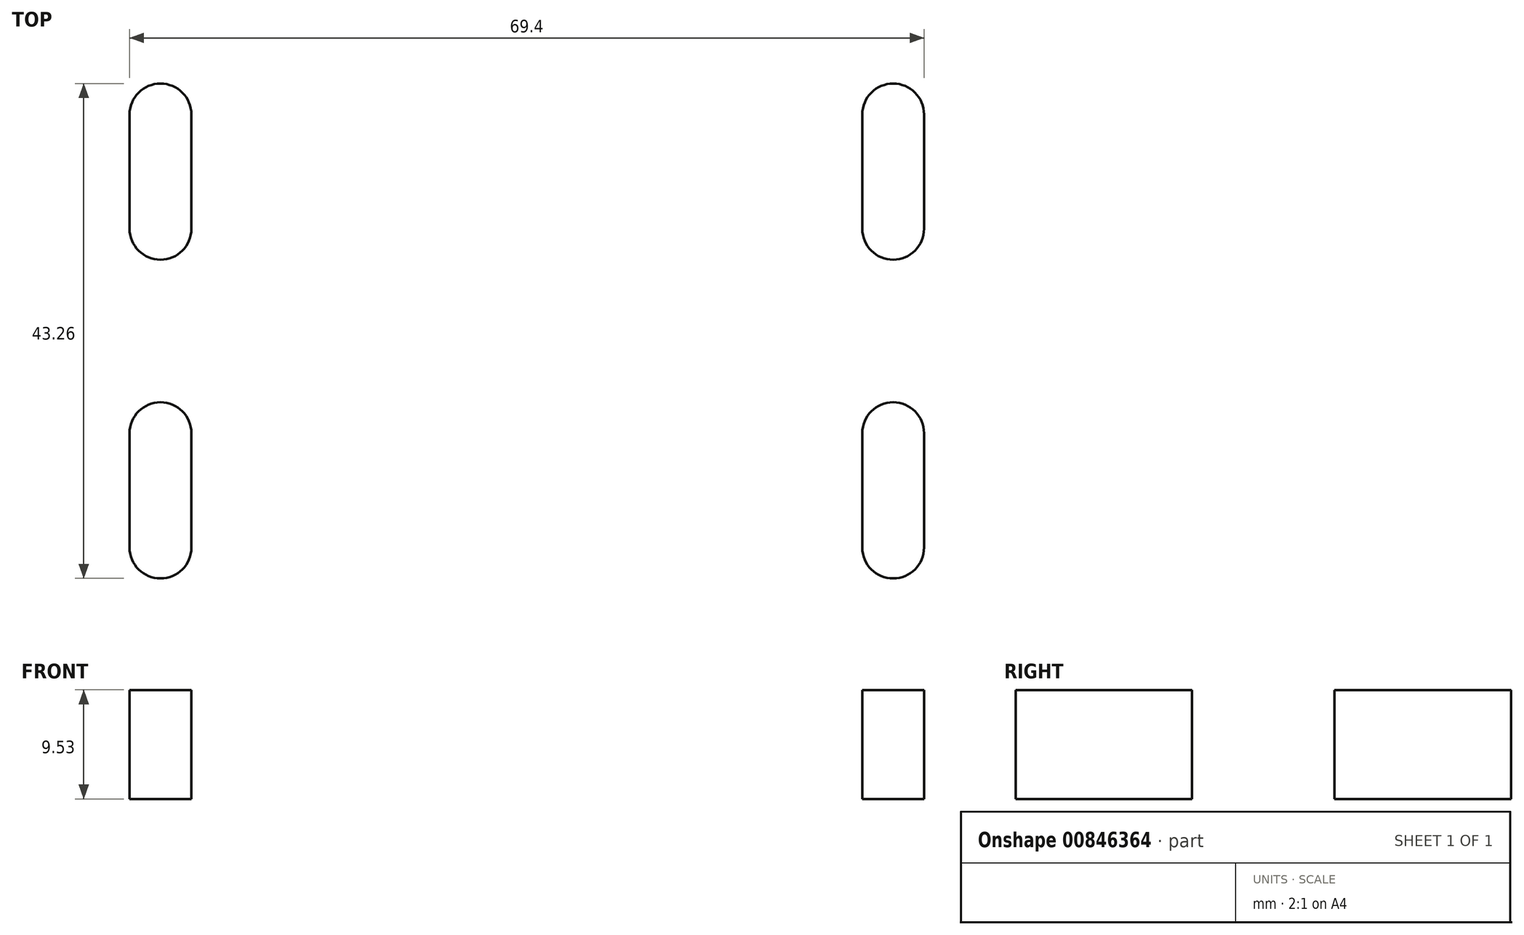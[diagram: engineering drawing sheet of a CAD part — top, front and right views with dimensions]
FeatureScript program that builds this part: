
annotation { "Feature Type Name" : "Feature", "Feature Type Description" : "" }
export const myFeature = defineFeature(function(context is Context, id is Id, definition is map)
    precondition{}
    {
        {
            var Q0;
            Q0=qCreatedBy(makeId("Top.planeOp"),FACE);
            var sketch = newSketch(context, id + "F0", { "sketchPlane" : qUnion([Q0])});
            skLineSegment(sketch, "E0.bottom", {"start": v(40, -25) * mm, "end": v(-40, -25) * mm});
            skLineSegment(sketch, "E0.top", {"start": v(40, 25) * mm, "end": v(-40, 25) * mm});
            skLineSegment(sketch, "E0.left", {"start": v(40, -25) * mm, "end": v(40, 25) * mm});
            skLineSegment(sketch, "E0.right", {"start": v(-40, -25) * mm, "end": v(-40, 25) * mm});
            skPoint(sketch, "E0.middle", {"position": v(0, 0) * mm});
            skSolve(sketch);
        }
        {
            var Q0;
            Q0=makeQuery(id+"F0.imprint","IMPRINT",FACE,{"disambiguationData":[TD([[makeQuery(id+"F0.imprint","IMPRINT",EDGE,{"derivedFrom":sQuery(id+"F0.wireOp",EDGE,"E0.bottom")}),-1.0]])]});
            extrude(context, id + "F1", {"entities" : qUnion([Q0]), "depth" : 9.52 * mm, "offsetDistance" : 25 * mm});
        }
        {
            var Q0;
            Q0=makeQuery(id+"F1.opExtrude","CAP_FACE",FACE,{"disambiguationData":[OSD([sQuery(id+"F0.wireOp",EDGE,"E0.bottom"),sQuery(id+"F0.wireOp",EDGE,"E0.top"),sQuery(id+"F0.wireOp",EDGE,"E0.left"),sQuery(id+"F0.wireOp",EDGE,"E0.right")])],"isStart":false});
            var sketch = newSketch(context, id + "F2", { "sketchPlane" : qUnion([Q0])});
            skLineSegment(sketch, "E1", {"start": v(-32, 18.93) * mm, "end": v(-32, 8.93) * mm});
            skLineSegment(sketch, "E2.MirrorCS", {"start": v(32, 18.93) * mm, "end": v(32, 8.93) * mm});
            skLineSegment(sketch, "E3.MirrorCS", {"start": v(-32, -18.93) * mm, "end": v(-32, -8.93) * mm});
            skLineSegment(sketch, "E4.MirrorCS", {"start": v(32, -18.93) * mm, "end": v(32, -8.93) * mm});
            skArc(sketch, "E5.0.startCap", {"start": v(-34.7, 18.93) * mm, "mid": v(-32, 21.63) * mm, "end": v(-29.3, 18.93) * mm});
            skArc(sketch, "E5.0.endCap", {"start": v(-29.3, 8.93) * mm, "mid": v(-32, 6.23) * mm, "end": v(-34.7, 8.93) * mm});
            skLineSegment(sketch, "E5.0.left", {"start": v(-29.3, 18.93) * mm, "end": v(-29.3, 8.93) * mm});
            skLineSegment(sketch, "E5.0.right", {"start": v(-34.7, 18.93) * mm, "end": v(-34.7, 8.93) * mm});
            skArc(sketch, "E6.0.startCap", {"start": v(29.3, 18.93) * mm, "mid": v(32, 21.63) * mm, "end": v(34.7, 18.93) * mm});
            skArc(sketch, "E6.0.endCap", {"start": v(34.7, 8.93) * mm, "mid": v(32, 6.23) * mm, "end": v(29.3, 8.93) * mm});
            skLineSegment(sketch, "E6.0.left", {"start": v(34.7, 18.93) * mm, "end": v(34.7, 8.93) * mm});
            skLineSegment(sketch, "E6.0.right", {"start": v(29.3, 18.93) * mm, "end": v(29.3, 8.93) * mm});
            skArc(sketch, "E6.1.startCap", {"start": v(34.7, -18.93) * mm, "mid": v(32, -21.63) * mm, "end": v(29.3, -18.93) * mm});
            skArc(sketch, "E6.1.endCap", {"start": v(29.3, -8.93) * mm, "mid": v(32, -6.23) * mm, "end": v(34.7, -8.93) * mm});
            skLineSegment(sketch, "E6.1.left", {"start": v(29.3, -18.93) * mm, "end": v(29.3, -8.93) * mm});
            skLineSegment(sketch, "E6.1.right", {"start": v(34.7, -18.93) * mm, "end": v(34.7, -8.93) * mm});
            skArc(sketch, "E6.2.startCap", {"start": v(-29.3, -18.93) * mm, "mid": v(-32, -21.63) * mm, "end": v(-34.7, -18.93) * mm});
            skArc(sketch, "E6.2.endCap", {"start": v(-34.7, -8.93) * mm, "mid": v(-32, -6.23) * mm, "end": v(-29.3, -8.93) * mm});
            skLineSegment(sketch, "E6.2.left", {"start": v(-34.7, -18.93) * mm, "end": v(-34.7, -8.93) * mm});
            skLineSegment(sketch, "E6.2.right", {"start": v(-29.3, -18.93) * mm, "end": v(-29.3, -8.93) * mm});
            skSolve(sketch);
        }
        {
            var Q0;
            Q0=makeQuery(id+"F2.imprint","IMPRINT",FACE,{"disambiguationData":[TD([[makeQuery(id+"F2.imprint","IMPRINT",EDGE,{"derivedFrom":sQuery(id+"F2.wireOp",EDGE,"E5.0.startCap")}),-1.0]])]});
            var Q1;
            Q1=makeQuery(id+"F2.imprint","IMPRINT",FACE,{"disambiguationData":[TD([[makeQuery(id+"F2.imprint","IMPRINT",EDGE,{"derivedFrom":sQuery(id+"F2.wireOp",EDGE,"E6.2.startCap")}),-1.0]])]});
            var Q2;
            Q2=makeQuery(id+"F2.imprint","IMPRINT",FACE,{"disambiguationData":[TD([[makeQuery(id+"F2.imprint","IMPRINT",EDGE,{"derivedFrom":sQuery(id+"F2.wireOp",EDGE,"E6.1.startCap")}),-1.0]])]});
            var Q3;
            Q3=makeQuery(id+"F2.imprint","IMPRINT",FACE,{"disambiguationData":[TD([[makeQuery(id+"F2.imprint","IMPRINT",EDGE,{"derivedFrom":sQuery(id+"F2.wireOp",EDGE,"E6.0.startCap")}),-1.0]])]});
            extrude(context, id + "F3", {"entities" : qUnion([Q0, Q1, Q2, Q3]), "operationType" : NewBodyOperationType.REMOVE, "oppositeDirection" : true, "depth" : 25 * mm, "offsetDistance" : 25 * mm});
        }
        {
            var Q0;
            Q0=makeQuery(id+"F1.opExtrude","CAP_FACE",FACE,{"disambiguationData":[OSD([sQuery(id+"F0.wireOp",EDGE,"E0.bottom"),sQuery(id+"F0.wireOp",EDGE,"E0.top"),sQuery(id+"F0.wireOp",EDGE,"E0.left"),sQuery(id+"F0.wireOp",EDGE,"E0.right")])],"isStart":false});
            var sketch = newSketch(context, id + "F4", { "sketchPlane" : qUnion([Q0])});
            skCircle(sketch, "E7", {"center": v(0, 4.68) * mm, "radius": 4.76 * mm});
            skSolve(sketch);
        }
        {
            var Q0;
            Q0=makeQuery(id+"F4.imprint","IMPRINT",FACE,{"disambiguationData":[TD([[makeQuery(id+"F4.imprint","IMPRINT",EDGE,{"derivedFrom":sQuery(id+"F4.wireOp",EDGE,"E7")}),1.0]])]});
            extrude(context, id + "F5", {"entities" : qUnion([Q0]), "operationType" : NewBodyOperationType.REMOVE, "endBound" : BoundingType.THROUGH_ALL, "oppositeDirection" : true, "depth" : 25 * mm, "offsetDistance" : 25 * mm});
        }
    });
